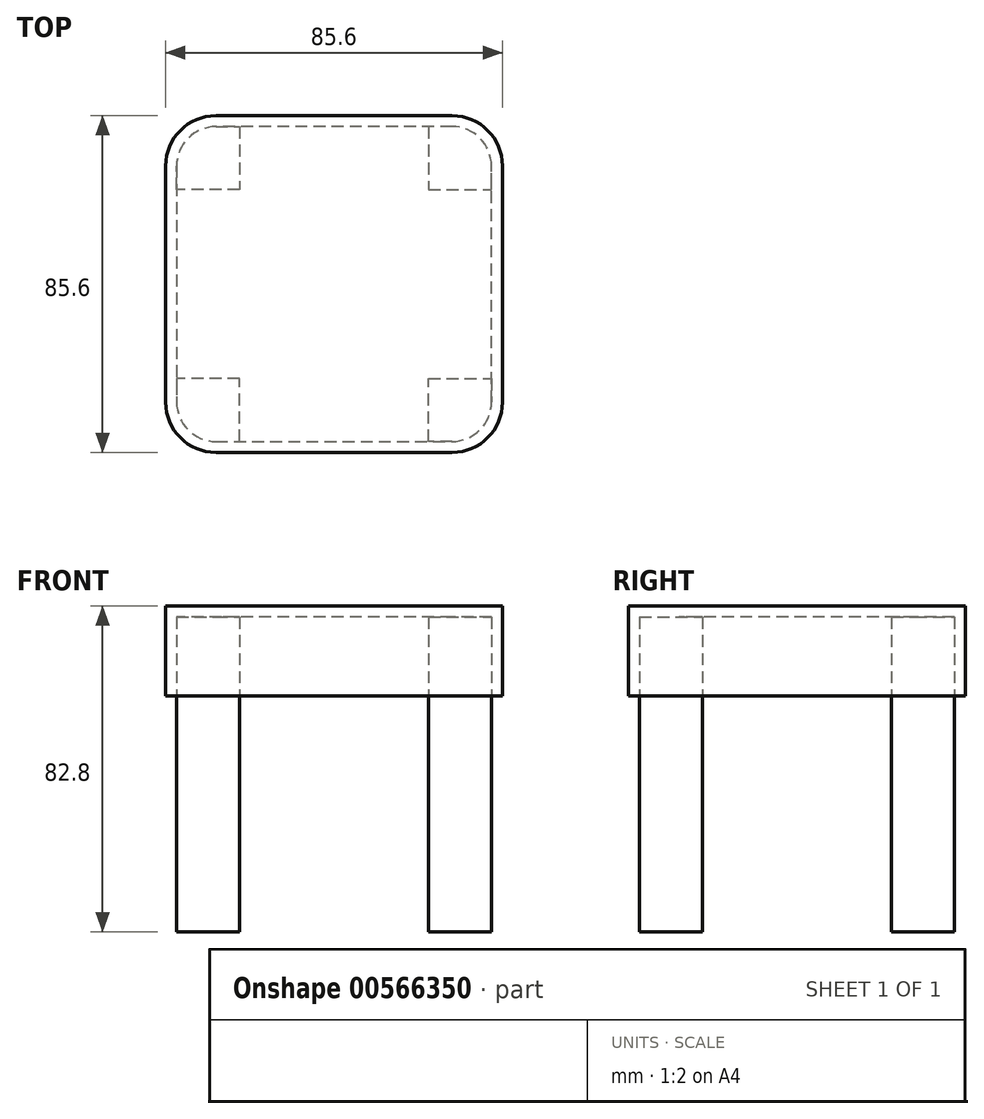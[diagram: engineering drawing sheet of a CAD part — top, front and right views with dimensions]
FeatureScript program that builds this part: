
annotation { "Feature Type Name" : "Feature", "Feature Type Description" : "" }
export const myFeature = defineFeature(function(context is Context, id is Id, definition is map)
    precondition{}
    {
        {
            var Q0;
            Q0=qCreatedBy(makeId("Top.planeOp"),FACE);
            var sketch = newSketch(context, id + "F0", { "sketchPlane" : qUnion([Q0])});
            skLineSegment(sketch, "E0", {"start": v(-40, 0) * mm, "end": v(40, 0) * mm, "construction": true});
            skLineSegment(sketch, "E1", {"start": v(40, 24) * mm, "end": v(40, -24) * mm, "construction": true});
            skLineSegment(sketch, "E2", {"start": v(40, 24) * mm, "end": v(40, 40) * mm});
            skLineSegment(sketch, "E3", {"start": v(40, 40) * mm, "end": v(24, 40) * mm});
            skLineSegment(sketch, "E4", {"start": v(24, 40) * mm, "end": v(24, 24) * mm});
            skLineSegment(sketch, "E5", {"start": v(24, 24) * mm, "end": v(40, 24) * mm});
            skLineSegment(sketch, "E6.MirrorCS", {"start": v(24, -24) * mm, "end": v(40, -24) * mm});
            skLineSegment(sketch, "E7.MirrorCS", {"start": v(24, -40) * mm, "end": v(24, -24) * mm});
            skLineSegment(sketch, "E8.MirrorCS", {"start": v(40, -40) * mm, "end": v(24, -40) * mm});
            skLineSegment(sketch, "E9.MirrorCS", {"start": v(40, -24) * mm, "end": v(40, -40) * mm});
            skLineSegment(sketch, "E10", {"start": v(0, 40) * mm, "end": v(0, -40) * mm, "construction": true});
            skLineSegment(sketch, "E11.MirrorCS", {"start": v(-24, -40) * mm, "end": v(-24, -24) * mm});
            skLineSegment(sketch, "E12.MirrorCS", {"start": v(-40, 24) * mm, "end": v(-40, -24) * mm, "construction": true});
            skLineSegment(sketch, "E13.MirrorCS", {"start": v(-24, 40) * mm, "end": v(-24, 24) * mm});
            skLineSegment(sketch, "E14.MirrorCS", {"start": v(-40, 40) * mm, "end": v(-24, 40) * mm});
            skLineSegment(sketch, "E15.MirrorCS", {"start": v(-24, 24) * mm, "end": v(-40, 24) * mm});
            skLineSegment(sketch, "E16.MirrorCS", {"start": v(-40, 24) * mm, "end": v(-40, 40) * mm});
            skLineSegment(sketch, "E17.MirrorCS", {"start": v(-40, -24) * mm, "end": v(-40, -40) * mm});
            skLineSegment(sketch, "E18.MirrorCS", {"start": v(-24, -24) * mm, "end": v(-40, -24) * mm});
            skLineSegment(sketch, "E19.MirrorCS", {"start": v(-40, -40) * mm, "end": v(-24, -40) * mm});
            skLineSegment(sketch, "E20", {"start": v(-24, 40) * mm, "end": v(24, 40) * mm, "construction": true});
            skLineSegment(sketch, "E21", {"start": v(-24, -40) * mm, "end": v(24, -40) * mm, "construction": true});
            skSolve(sketch);
        }
        {
            var Q0;
            Q0=makeQuery(id+"F0.imprint","IMPRINT",FACE,{"disambiguationData":[TD([[makeQuery(id+"F0.imprint","IMPRINT",EDGE,{"derivedFrom":sQuery(id+"F0.wireOp",EDGE,"E13.MirrorCS")}),-1.0]])]});
            var Q1;
            Q1=makeQuery(id+"F0.imprint","IMPRINT",FACE,{"disambiguationData":[TD([[makeQuery(id+"F0.imprint","IMPRINT",EDGE,{"derivedFrom":sQuery(id+"F0.wireOp",EDGE,"E2")}),1.0]])]});
            var Q2;
            Q2=makeQuery(id+"F0.imprint","IMPRINT",FACE,{"disambiguationData":[TD([[makeQuery(id+"F0.imprint","IMPRINT",EDGE,{"derivedFrom":sQuery(id+"F0.wireOp",EDGE,"E6.MirrorCS")}),-1.0]])]});
            var Q3;
            Q3=makeQuery(id+"F0.imprint","IMPRINT",FACE,{"disambiguationData":[TD([[makeQuery(id+"F0.imprint","IMPRINT",EDGE,{"derivedFrom":sQuery(id+"F0.wireOp",EDGE,"E11.MirrorCS")}),1.0]])]});
            extrude(context, id + "F1", {"entities" : qUnion([Q0, Q1, Q2, Q3]), "depth" : 80 * mm, "offsetDistance" : 25 * mm});
        }
        {
            var Q0;
            Q0=qCreatedBy(makeId("Top.planeOp"),FACE);
            var sketch = newSketch(context, id + "F2", { "sketchPlane" : qUnion([Q0])});
            skLineSegment(sketch, "E22", {"start": v(0, 40) * mm, "end": v(0, -40) * mm, "construction": true});
            skLineSegment(sketch, "E23", {"start": v(40, 0) * mm, "end": v(-40, 0) * mm, "construction": true});
            skLineSegment(sketch, "E24", {"start": v(-40, 40) * mm, "end": v(-40, -40) * mm});
            skLineSegment(sketch, "E25", {"start": v(-40, -40) * mm, "end": v(40, -40) * mm});
            skLineSegment(sketch, "E26", {"start": v(40, -40) * mm, "end": v(40, 40) * mm});
            skLineSegment(sketch, "E27", {"start": v(40, 40) * mm, "end": v(-40, 40) * mm});
            skSolve(sketch);
        }
        {
            var Q0;
            Q0 = qSketchRegion(id + "F2", true);
            extrude(context, id + "F3", {"entities" : qUnion([Q0]), "depth" : 80 * mm, "offsetDistance" : 25 * mm, "hasSecondDirection" : true, "secondDirectionOppositeDirection" : false, "secondDirectionDepth" : 60 * mm});
        }
        {
            var Q0;
            Q0=makeQuery(id+"F3.opExtrude","SWEPT_EDGE",EDGE,{"disambiguationData":[OSD([sQuery(id+"F2.wireOp",EDGE,"E24"),sQuery(id+"F2.wireOp",EDGE,"E25")])]});
            var Q1;
            Q1=makeQuery(id+"F3.opExtrude","SWEPT_EDGE",EDGE,{"disambiguationData":[OSD([sQuery(id+"F2.wireOp",EDGE,"E25"),sQuery(id+"F2.wireOp",EDGE,"E26")])]});
            var Q2;
            Q2=makeQuery(id+"F3.opExtrude","SWEPT_EDGE",EDGE,{"disambiguationData":[OSD([sQuery(id+"F2.wireOp",EDGE,"E26"),sQuery(id+"F2.wireOp",EDGE,"E27")])]});
            var Q3;
            Q3=makeQuery(id+"F1.opExtrude","SWEPT_EDGE",EDGE,{"disambiguationData":[OSD([sQuery(id+"F0.wireOp",EDGE,"E2"),sQuery(id+"F0.wireOp",EDGE,"E3")])]});
            var Q4;
            Q4=makeQuery(id+"F1.opExtrude","SWEPT_EDGE",EDGE,{"disambiguationData":[OSD([sQuery(id+"F0.wireOp",EDGE,"E8.MirrorCS"),sQuery(id+"F0.wireOp",EDGE,"E9.MirrorCS")])]});
            var Q5;
            Q5=makeQuery(id+"F1.opExtrude","SWEPT_EDGE",EDGE,{"disambiguationData":[OSD([sQuery(id+"F0.wireOp",EDGE,"E17.MirrorCS"),sQuery(id+"F0.wireOp",EDGE,"E19.MirrorCS")])]});
            var Q6;
            Q6=makeQuery(id+"F1.opExtrude","SWEPT_EDGE",EDGE,{"disambiguationData":[OSD([sQuery(id+"F0.wireOp",EDGE,"E14.MirrorCS"),sQuery(id+"F0.wireOp",EDGE,"E16.MirrorCS")])]});
            var Q7;
            Q7=makeQuery(id+"F3.opExtrude","SWEPT_EDGE",EDGE,{"disambiguationData":[OSD([sQuery(id+"F2.wireOp",EDGE,"E24"),sQuery(id+"F2.wireOp",EDGE,"E27")])]});
            fillet(context, id + "F4", {"entities" : qUnion([Q0, Q1, Q2, Q3, Q4, Q5, Q6, Q7]), "radius" : 10 * mm, "tangentPropagation" : true, "allowEdgeOverflow" : false});
        }
        {
            var Q0;
            Q0=makeQuery(id+"F3.opExtrude","CAP_FACE",FACE,{"disambiguationData":[OSD([sQuery(id+"F2.wireOp",EDGE,"E24"),sQuery(id+"F2.wireOp",EDGE,"E25"),sQuery(id+"F2.wireOp",EDGE,"E26"),sQuery(id+"F2.wireOp",EDGE,"E27")])],"isStart":true});
            shell(context, id + "F5", {"entities" : qUnion([Q0]), "thickness" : 2.8 * mm, "oppositeDirection" : true});
        }
    });
